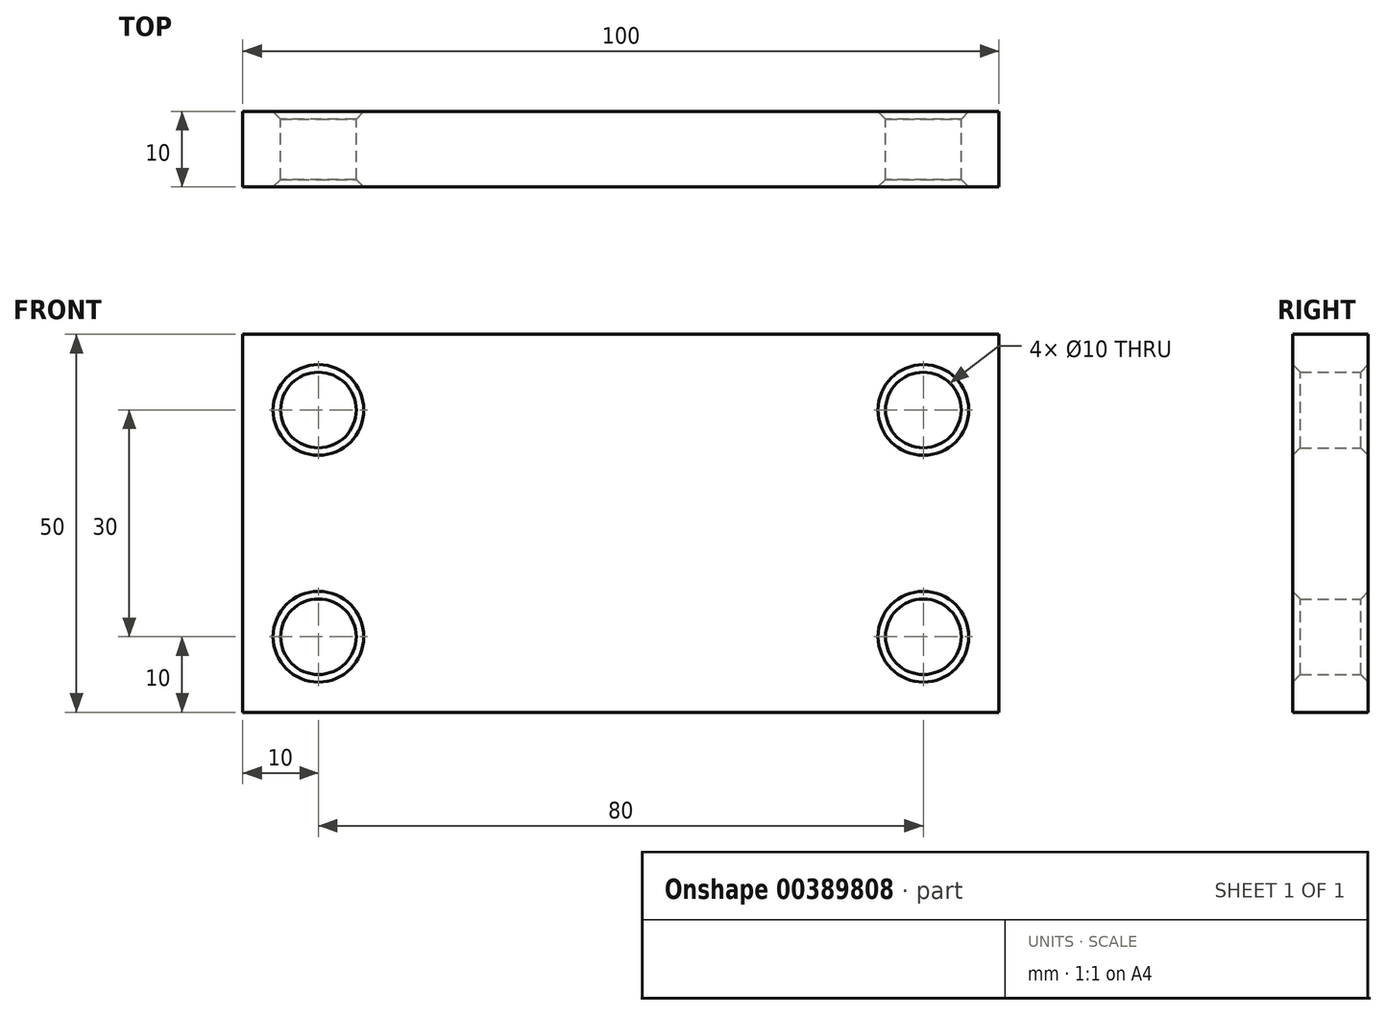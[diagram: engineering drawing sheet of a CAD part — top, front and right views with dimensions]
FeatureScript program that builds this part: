
annotation { "Feature Type Name" : "Feature", "Feature Type Description" : "" }
export const myFeature = defineFeature(function(context is Context, id is Id, definition is map)
    precondition{}
    {
        {
            var Q0;
            Q0=qCreatedBy(makeId("Front.planeOp"),FACE);
            var sketch = newSketch(context, id + "F0", { "sketchPlane" : qUnion([Q0])});
            skLineSegment(sketch, "E0.bottom", {"start": v(50, 25) * mm, "end": v(-50, 25) * mm});
            skLineSegment(sketch, "E0.top", {"start": v(50, -25) * mm, "end": v(-50, -25) * mm});
            skLineSegment(sketch, "E0.left", {"start": v(50, 25) * mm, "end": v(50, -25) * mm});
            skLineSegment(sketch, "E0.right", {"start": v(-50, 25) * mm, "end": v(-50, -25) * mm});
            skPoint(sketch, "E0.middle", {"position": v(0, 0) * mm});
            skCircle(sketch, "E1", {"center": v(-40, 15) * mm, "radius": 5 * mm});
            skCircle(sketch, "E2.MirrorC", {"center": v(40, 15) * mm, "radius": 5 * mm});
            skCircle(sketch, "E3.MirrorC", {"center": v(-40, -15) * mm, "radius": 5 * mm});
            skCircle(sketch, "E4.MirrorC", {"center": v(40, -15) * mm, "radius": 5 * mm});
            skSolve(sketch);
        }
        {
            var Q0;
            Q0=makeQuery(id+"F0.imprint","IMPRINT",FACE,{"disambiguationData":[TD([[makeQuery(id+"F0.imprint","IMPRINT",EDGE,{"derivedFrom":sQuery(id+"F0.wireOp",EDGE,"E0.bottom")}),1.0]])]});
            extrude(context, id + "F1", {"entities" : qUnion([Q0]), "depth" : 10 * mm});
        }
        {
            var Q0;
            Q0=makeQuery(id+"F1.opExtrude","CAP_EDGE",EDGE,{"disambiguationData":[OSD([sQuery(id+"F0.wireOp",EDGE,"E1")])],"isStart":false});
            var Q1;
            Q1=makeQuery(id+"F1.opExtrude","CAP_EDGE",EDGE,{"disambiguationData":[OSD([sQuery(id+"F0.wireOp",EDGE,"E3.MirrorC")])],"isStart":false});
            chamfer(context, id + "F2", {"entities" : qUnion([Q0, Q1]), "width" : 1 * mm, "tangentPropagation" : true});
        }
        {
            var Q0;
            Q0=makeQuery(id+"F1.opExtrude","CAP_EDGE",EDGE,{"disambiguationData":[OSD([sQuery(id+"F0.wireOp",EDGE,"E2.MirrorC")])],"isStart":false});
            var Q1;
            Q1=makeQuery(id+"F1.opExtrude","CAP_EDGE",EDGE,{"disambiguationData":[OSD([sQuery(id+"F0.wireOp",EDGE,"E2.MirrorC")])],"isStart":false});
            var Q2;
            Q2=makeQuery(id+"F1.opExtrude","CAP_EDGE",EDGE,{"disambiguationData":[OSD([sQuery(id+"F0.wireOp",EDGE,"E4.MirrorC")])],"isStart":false});
            chamfer(context, id + "F3", {"entities" : qUnion([Q0, Q1, Q2]), "width" : 1 * mm, "tangentPropagation" : true});
        }
        {
            var Q0;
            Q0=makeQuery(id+"F1.opExtrude","CAP_EDGE",EDGE,{"disambiguationData":[OSD([sQuery(id+"F0.wireOp",EDGE,"E2.MirrorC")])],"isStart":true});
            var Q1;
            Q1=makeQuery(id+"F1.opExtrude","CAP_EDGE",EDGE,{"disambiguationData":[OSD([sQuery(id+"F0.wireOp",EDGE,"E1")])],"isStart":true});
            var Q2;
            Q2=makeQuery(id+"F1.opExtrude","CAP_EDGE",EDGE,{"disambiguationData":[OSD([sQuery(id+"F0.wireOp",EDGE,"E3.MirrorC")])],"isStart":true});
            var Q3;
            Q3=makeQuery(id+"F1.opExtrude","CAP_EDGE",EDGE,{"disambiguationData":[OSD([sQuery(id+"F0.wireOp",EDGE,"E4.MirrorC")])],"isStart":true});
            chamfer(context, id + "F4", {"entities" : qUnion([Q0, Q1, Q2, Q3]), "width" : 1 * mm, "tangentPropagation" : true});
        }
    });
